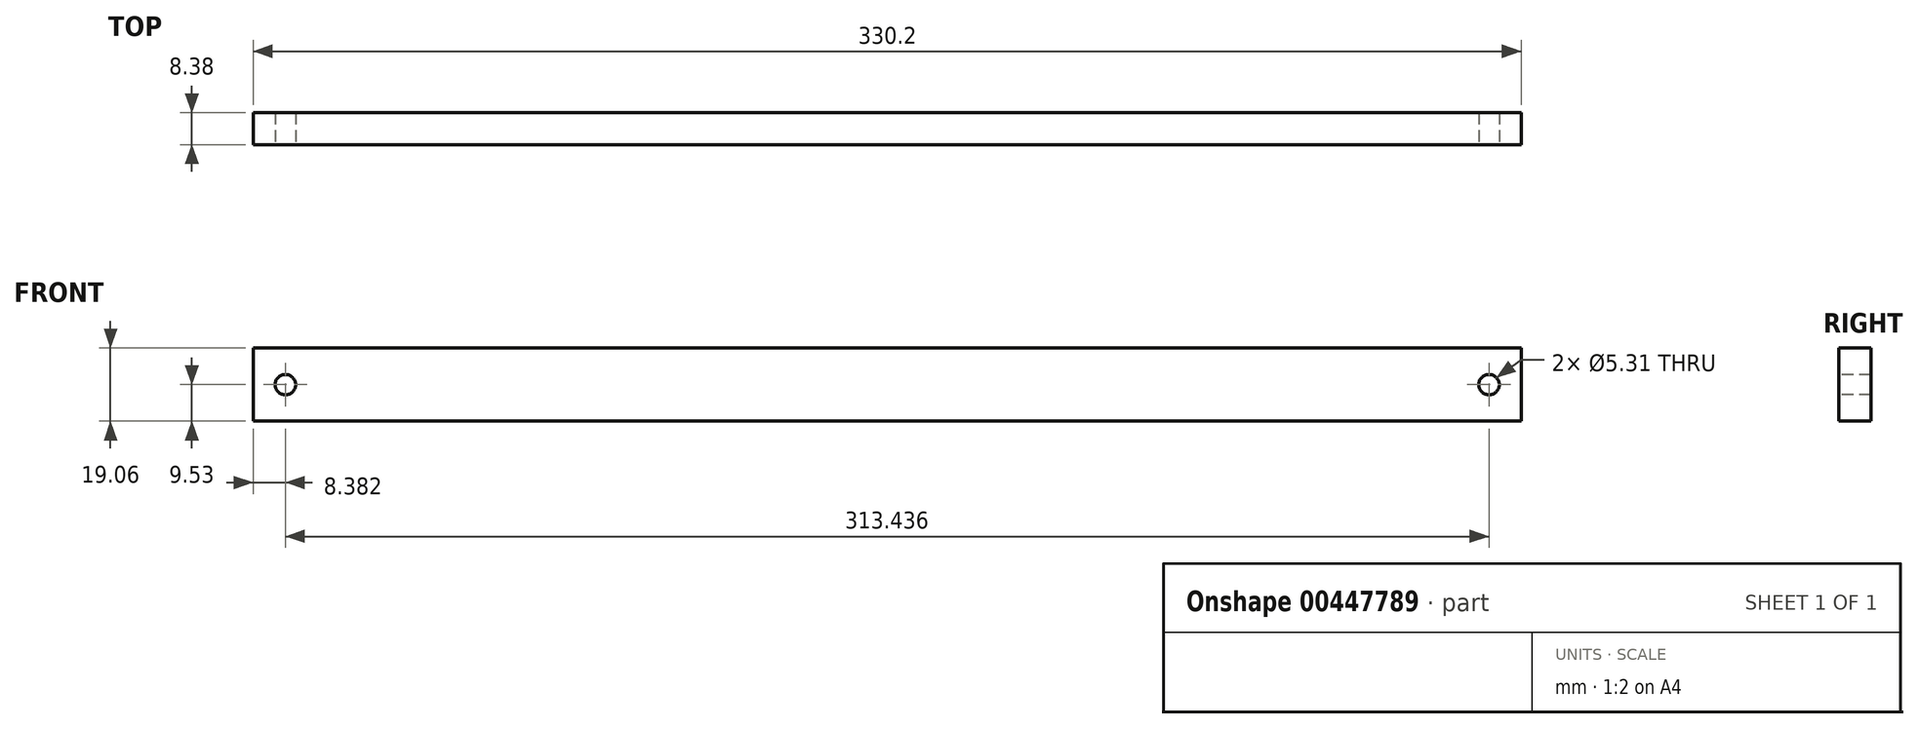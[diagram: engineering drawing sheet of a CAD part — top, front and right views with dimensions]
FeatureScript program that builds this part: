
annotation { "Feature Type Name" : "Feature", "Feature Type Description" : "" }
export const myFeature = defineFeature(function(context is Context, id is Id, definition is map)
    precondition{}
    {
        {
            var Q0;
            Q0=qCreatedBy(makeId("Front.planeOp"),FACE);
            var sketch = newSketch(context, id + "F0", { "sketchPlane" : qUnion([Q0])});
            skLineSegment(sketch, "E0.bottom", {"start": v(165.1, -9.52) * mm, "end": v(-165.1, -9.52) * mm});
            skLineSegment(sketch, "E0.top", {"start": v(165.1, 9.53) * mm, "end": v(-165.1, 9.53) * mm});
            skLineSegment(sketch, "E0.left", {"start": v(165.1, -9.52) * mm, "end": v(165.1, 9.53) * mm});
            skLineSegment(sketch, "E0.right", {"start": v(-165.1, -9.52) * mm, "end": v(-165.1, 9.53) * mm});
            skPoint(sketch, "E0.middle", {"position": v(0, 0) * mm});
            skPoint(sketch, "E1", {"position": v(-156.72, 0) * mm});
            skPoint(sketch, "E2", {"position": v(156.72, 0) * mm});
            skSolve(sketch);
        }
        {
            var Q0;
            Q0=makeQuery(id+"F0.imprint","IMPRINT",FACE,{"disambiguationData":[TD([[makeQuery(id+"F0.imprint","IMPRINT",EDGE,{"derivedFrom":sQuery(id+"F0.wireOp",EDGE,"E0.bottom")}),-1.0]])]});
            extrude(context, id + "F1", {"entities" : qUnion([Q0]), "depth" : 8.38 * mm, "symmetric" : true});
        }
        {
            var Q0;
            Q0=sQuery(id+"F0.wireOp",VERTEX,"E1");
            var Q1;
            Q1=sQuery(id+"F0.wireOp",VERTEX,"E2");
            var Q2;
            Q2=makeQuery(id+"F1.opExtrude","SWEPT_BODY",BODY,{"disambiguationData":[OSD([sQuery(id+"F0.wireOp",EDGE,"E0.bottom"),sQuery(id+"F0.wireOp",EDGE,"E0.top"),sQuery(id+"F0.wireOp",EDGE,"E0.left"),sQuery(id+"F0.wireOp",EDGE,"E0.right")])]});
            hole(context, id + "F2", {"style" : HoleStyle.SIMPLE, "endStyle" : HoleEndStyle.THROUGH, "standardTappedOrClearance" : lookupTablePath({ "standard" : "ANSI", "size" : "#4 (0.2)", "type" : "Drilled" }), "standardBlindInLast" : lookupTablePath({ "standard" : "ANSI", "size" : "#4", "type" : "Drilled" }), "holeDiameter" : 5.3 * mm, "isTappedThrough" : true, "tappedDepth" : 12.7 * mm, "tapClearance" : 3, "startFromSketch" : true, "locations" : qUnion([Q0, Q1]), "scope" : qUnion([Q2])});
        }
        {
            var Q0;
            Q0=sQuery(id+"F0.wireOp",VERTEX,"E1");
            var Q1;
            Q1=sQuery(id+"F0.wireOp",VERTEX,"E2");
            var Q2;
            Q2=makeQuery(id+"F1.opExtrude","SWEPT_BODY",BODY,{"disambiguationData":[OSD([sQuery(id+"F0.wireOp",EDGE,"E0.bottom"),sQuery(id+"F0.wireOp",EDGE,"E0.top"),sQuery(id+"F0.wireOp",EDGE,"E0.left"),sQuery(id+"F0.wireOp",EDGE,"E0.right")])]});
            hole(context, id + "F3", {"style" : HoleStyle.SIMPLE, "endStyle" : HoleEndStyle.THROUGH, "oppositeDirection" : true, "standardTappedOrClearance" : lookupTablePath({ "standard" : "ANSI", "size" : "#4 (0.2)", "type" : "Drilled" }), "standardBlindInLast" : lookupTablePath({ "standard" : "ANSI", "size" : "#4", "type" : "Drilled" }), "holeDiameter" : 5.3 * mm, "isTappedThrough" : true, "tappedDepth" : 12.7 * mm, "tapClearance" : 3, "startFromSketch" : true, "locations" : qUnion([Q0, Q1]), "scope" : qUnion([Q2])});
        }
    });
